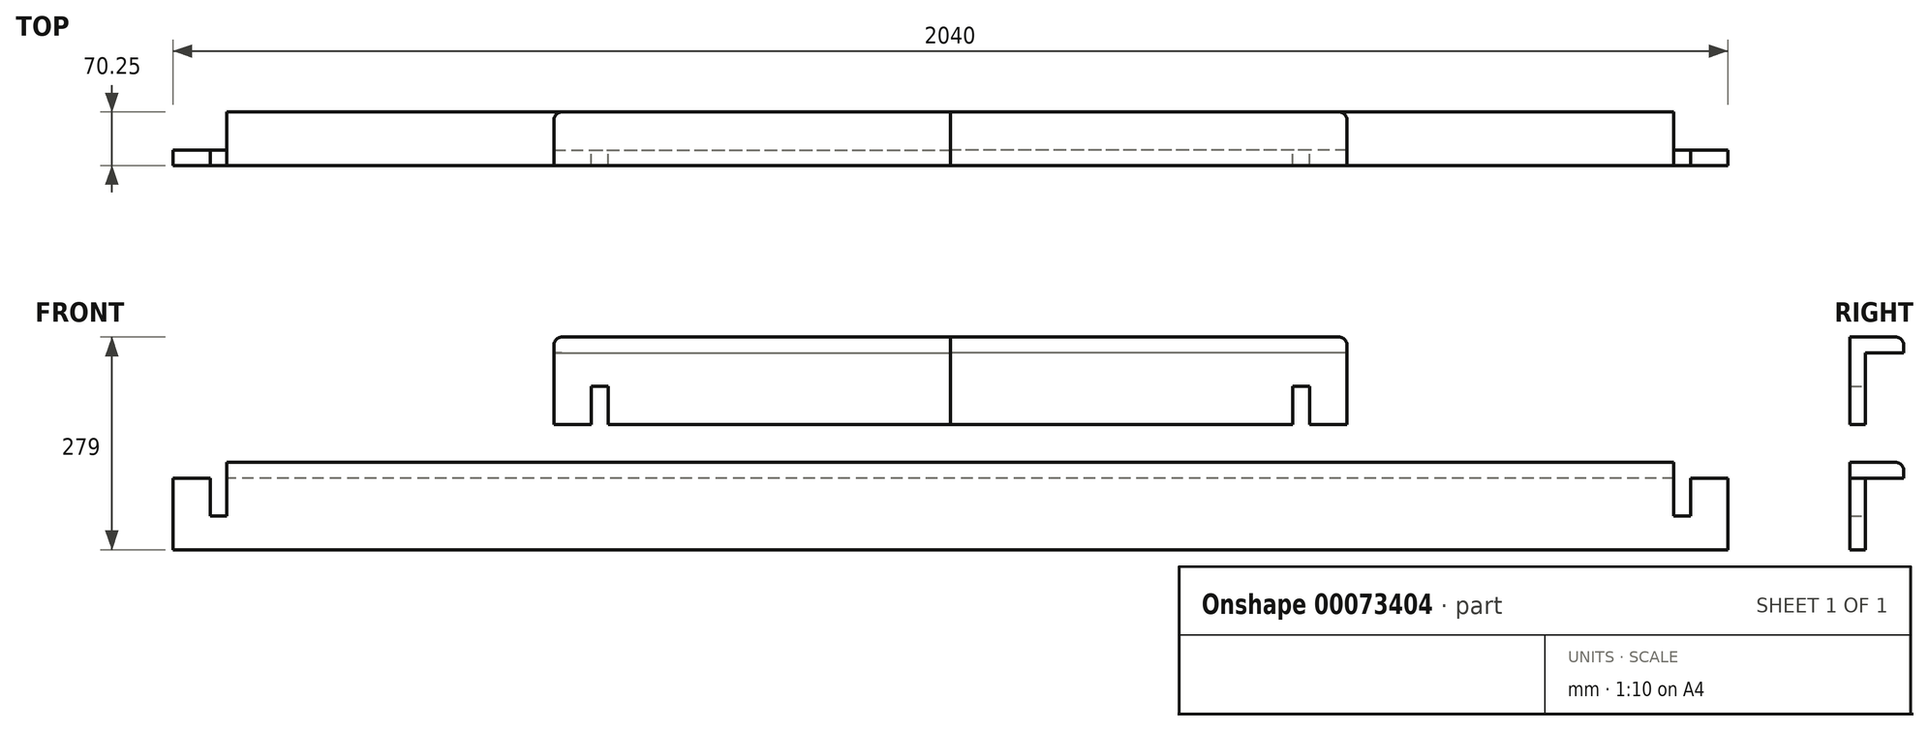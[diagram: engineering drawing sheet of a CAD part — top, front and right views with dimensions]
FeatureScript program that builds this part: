
annotation { "Feature Type Name" : "Feature", "Feature Type Description" : "" }
export const myFeature = defineFeature(function(context is Context, id is Id, definition is map)
    precondition{}
    {
        {
            var Q0;
            Q0=qCreatedBy(makeId("Right.planeOp"),FACE);
            var sketch = newSketch(context, id + "F0", { "sketchPlane" : qUnion([Q0])});
            skLineSegment(sketch, "E0", {"start": v(0, 0) * mm, "end": v(0, -114.5) * mm});
            skLineSegment(sketch, "E1", {"start": v(0, -114.5) * mm, "end": v(20.5, -114.5) * mm});
            skLineSegment(sketch, "E2", {"start": v(20.5, -114.5) * mm, "end": v(20.5, -20.5) * mm});
            skLineSegment(sketch, "E3", {"start": v(20.5, -20.5) * mm, "end": v(70.25, -20.5) * mm});
            skLineSegment(sketch, "E4", {"start": v(70.25, -20.5) * mm, "end": v(70.25, 0) * mm});
            skLineSegment(sketch, "E5", {"start": v(70.25, 0) * mm, "end": v(0, 0) * mm});
            skLineSegment(sketch, "E6", {"start": v(0, 164.5) * mm, "end": v(0, 50) * mm});
            skLineSegment(sketch, "E7", {"start": v(0, 50) * mm, "end": v(20.5, 50) * mm});
            skLineSegment(sketch, "E8", {"start": v(20.5, 50) * mm, "end": v(20.5, 144) * mm});
            skLineSegment(sketch, "E9", {"start": v(20.5, 144) * mm, "end": v(70.25, 144) * mm});
            skLineSegment(sketch, "E10", {"start": v(70.25, 144) * mm, "end": v(70.25, 164.5) * mm});
            skLineSegment(sketch, "E11", {"start": v(70.25, 164.5) * mm, "end": v(0, 164.5) * mm});
            skLineSegment(sketch, "E12", {"start": v(10.25, -114.5) * mm, "end": v(10.25, 0) * mm, "construction": true});
            skSolve(sketch);
        }
        {
            var Q0;
            Q0=makeQuery(id+"F0.imprint","IMPRINT",FACE,{"disambiguationData":[TD([[makeQuery(id+"F0.imprint","IMPRINT",EDGE,{"derivedFrom":sQuery(id+"F0.wireOp",EDGE,"E0")}),1.0]])]});
            extrude(context, id + "F1", {"entities" : qUnion([Q0]), "depth" : 1020 * mm});
        }
        {
            var Q0;
            Q0=makeQuery(id+"F1.opExtrude","SWEPT_FACE",FACE,{"disambiguationData":[OSD([sQuery(id+"F0.wireOp",EDGE,"E4")])]});
            var sketch = newSketch(context, id + "F2", { "sketchPlane" : qUnion([Q0])});
            skLineSegment(sketch, "E13.0", {"start": v(-1020, -114.5) * mm, "end": v(-1020, -20.5) * mm});
            skLineSegment(sketch, "E13.1", {"start": v(-1020, -20.5) * mm, "end": v(0, -20.5) * mm});
            skLineSegment(sketch, "E14.0", {"start": v(-1020, 0) * mm, "end": v(0, 0) * mm});
            skLineSegment(sketch, "E15", {"start": v(-949, 0) * mm, "end": v(-949, -20.5) * mm});
            skLineSegment(sketch, "E16", {"start": v(-949, -20.5) * mm, "end": v(-949, -70.5) * mm});
            skLineSegment(sketch, "E17", {"start": v(-949, -70.5) * mm, "end": v(-971, -70.5) * mm});
            skLineSegment(sketch, "E18", {"start": v(-971, -70.5) * mm, "end": v(-971, -20.5) * mm});
            skLineSegment(sketch, "E19.0", {"start": v(-1020, -20.5) * mm, "end": v(-1020, 0) * mm});
            skLineSegment(sketch, "E20", {"start": v(-960, -70.5) * mm, "end": v(-960, -46.2) * mm, "construction": true});
            skSolve(sketch);
        }
        {
            var Q0;
            {var subQ0=sQuery(id+"F2.wireOp",EDGE,"E15");Q0=makeQuery(id+"F2.imprint","IMPRINT",FACE,{"disambiguationData":[TD([[makeQuery(id+"F2.imprint","IMPRINT",EDGE,{"derivedFrom":subQ0}),-1.0]])]});}
            var Q1;
            {var subQ0=sQuery(id+"F2.wireOp",EDGE,"E16");Q1=makeQuery(id+"F2.imprint","IMPRINT",FACE,{"disambiguationData":[TD([[makeQuery(id+"F2.imprint","IMPRINT",EDGE,{"derivedFrom":subQ0}),-1.0]])]});}
            extrude(context, id + "F3", {"entities" : qUnion([Q0, Q1]), "operationType" : NewBodyOperationType.REMOVE, "oppositeDirection" : true, "depth" : 100 * mm});
        }
        {
            var Q0;
            Q0=makeQuery(id+"F1.opExtrude","SWEPT_BODY",BODY,{"disambiguationData":[OSD([sQuery(id+"F0.wireOp",EDGE,"E0"),sQuery(id+"F0.wireOp",EDGE,"E1"),sQuery(id+"F0.wireOp",EDGE,"E2"),sQuery(id+"F0.wireOp",EDGE,"E3"),sQuery(id+"F0.wireOp",EDGE,"E4"),sQuery(id+"F0.wireOp",EDGE,"E5")])]});
            var Q1;
            Q1=qCreatedBy(makeId("Right.planeOp"),FACE);
            mirror(context, id + "F4", {"operationType" : NewBodyOperationType.ADD, "entities" : qUnion([Q0]), "mirrorPlane" : qUnion([Q1])});
        }
        {
            var Q0;
            Q0=makeQuery(id+"F0.imprint","IMPRINT",FACE,{"disambiguationData":[TD([[makeQuery(id+"F0.imprint","IMPRINT",EDGE,{"derivedFrom":sQuery(id+"F0.wireOp",EDGE,"E6")}),1.0]])]});
            extrude(context, id + "F5", {"entities" : qUnion([Q0]), "depth" : 520 * mm});
        }
        {
            var Q0;
            Q0=makeQuery(id+"F5.opExtrude","SWEPT_FACE",FACE,{"disambiguationData":[OSD([sQuery(id+"F0.wireOp",EDGE,"E8")])]});
            var sketch = newSketch(context, id + "F6", { "sketchPlane" : qUnion([Q0])});
            skLineSegment(sketch, "E21.0", {"start": v(-520, 50) * mm, "end": v(0, 50) * mm});
            skLineSegment(sketch, "E22", {"start": v(-471, 50) * mm, "end": v(-471, 100) * mm});
            skLineSegment(sketch, "E23", {"start": v(-471, 100) * mm, "end": v(-449, 100) * mm});
            skLineSegment(sketch, "E24", {"start": v(-449, 100) * mm, "end": v(-449, 50) * mm});
            skLineSegment(sketch, "E25", {"start": v(-460, 100) * mm, "end": v(-460, 58.43) * mm, "construction": true});
            skSolve(sketch);
        }
        {
            var Q0;
            {var subQ0=sQuery(id+"F6.wireOp",EDGE,"E22");Q0=makeQuery(id+"F6.imprint","IMPRINT",FACE,{"disambiguationData":[TD([[makeQuery(id+"F6.imprint","IMPRINT",EDGE,{"derivedFrom":subQ0}),-1.0]])]});}
            extrude(context, id + "F7", {"entities" : qUnion([Q0]), "operationType" : NewBodyOperationType.REMOVE, "endBound" : BoundingType.UP_TO_NEXT, "oppositeDirection" : true, "depth" : 25 * mm});
        }
        {
            var Q0;
            Q0=makeQuery(id+"F5.opExtrude","SWEPT_BODY",BODY,{"disambiguationData":[OSD([sQuery(id+"F0.wireOp",EDGE,"E6"),sQuery(id+"F0.wireOp",EDGE,"E7"),sQuery(id+"F0.wireOp",EDGE,"E8"),sQuery(id+"F0.wireOp",EDGE,"E9"),sQuery(id+"F0.wireOp",EDGE,"E10"),sQuery(id+"F0.wireOp",EDGE,"E11")])]});
            var Q1;
            Q1=makeQuery(id+"F0.imprint","IMPRINT",FACE,{"disambiguationData":[TD([[makeQuery(id+"F0.imprint","IMPRINT",EDGE,{"derivedFrom":sQuery(id+"F0.wireOp",EDGE,"E6")}),1.0]])]});
            mirror(context, id + "F8", {"operationType" : NewBodyOperationType.ADD, "entities" : qUnion([Q0]), "mirrorPlane" : qUnion([Q1])});
        }
        {
            var Q0;
            {var subQ0=makeQuery(id+"F1.opExtrude","SWEPT_EDGE",EDGE,{"disambiguationData":[OSD([sQuery(id+"F0.wireOp",EDGE,"E4"),sQuery(id+"F0.wireOp",EDGE,"E5")])]});Q0=makeQuery(id+"F4.boolean.opBoolean","MERGE",EDGE,{"derivedFrom":[subQ0,makeQuery(id+"F4.opPattern","COPY",EDGE,{"derivedFrom":subQ0,"instanceName":"1"})]});}
            fillet(context, id + "F9", {"entities" : qUnion([Q0]), "radius" : 10 * mm, "tangentPropagation" : true, "allowEdgeOverflow" : false});
        }
        {
            var Q0;
            {var subQ0=makeQuery(id+"F5.opExtrude","SWEPT_EDGE",EDGE,{"disambiguationData":[OSD([sQuery(id+"F0.wireOp",EDGE,"E10"),sQuery(id+"F0.wireOp",EDGE,"E11")])]});Q0=makeQuery(id+"F8.boolean.opBoolean","MERGE",EDGE,{"derivedFrom":[subQ0,makeQuery(id+"F8.opPattern","COPY",EDGE,{"derivedFrom":subQ0,"instanceName":"1"})]});}
            var Q1;
            Q1=makeQuery(id+"F8.opPattern","COPY",EDGE,{"derivedFrom":makeQuery(id+"F5.opExtrude","CAP_EDGE",EDGE,{"disambiguationData":[OSD([sQuery(id+"F0.wireOp",EDGE,"E11")])],"isStart":false}),"instanceName":"1"});
            var Q2;
            Q2=makeQuery(id+"F8.opPattern","COPY",EDGE,{"derivedFrom":makeQuery(id+"F5.opExtrude","CAP_EDGE",EDGE,{"disambiguationData":[OSD([sQuery(id+"F0.wireOp",EDGE,"E10")])],"isStart":false}),"instanceName":"1"});
            var Q3;
            Q3=makeQuery(id+"F5.opExtrude","CAP_EDGE",EDGE,{"disambiguationData":[OSD([sQuery(id+"F0.wireOp",EDGE,"E11")])],"isStart":false});
            var Q4;
            Q4=makeQuery(id+"F5.opExtrude","CAP_EDGE",EDGE,{"disambiguationData":[OSD([sQuery(id+"F0.wireOp",EDGE,"E10")])],"isStart":false});
            fillet(context, id + "F10", {"entities" : qUnion([Q0, Q1, Q2, Q3, Q4]), "radius" : 10 * mm, "tangentPropagation" : true, "allowEdgeOverflow" : false});
        }
    });
